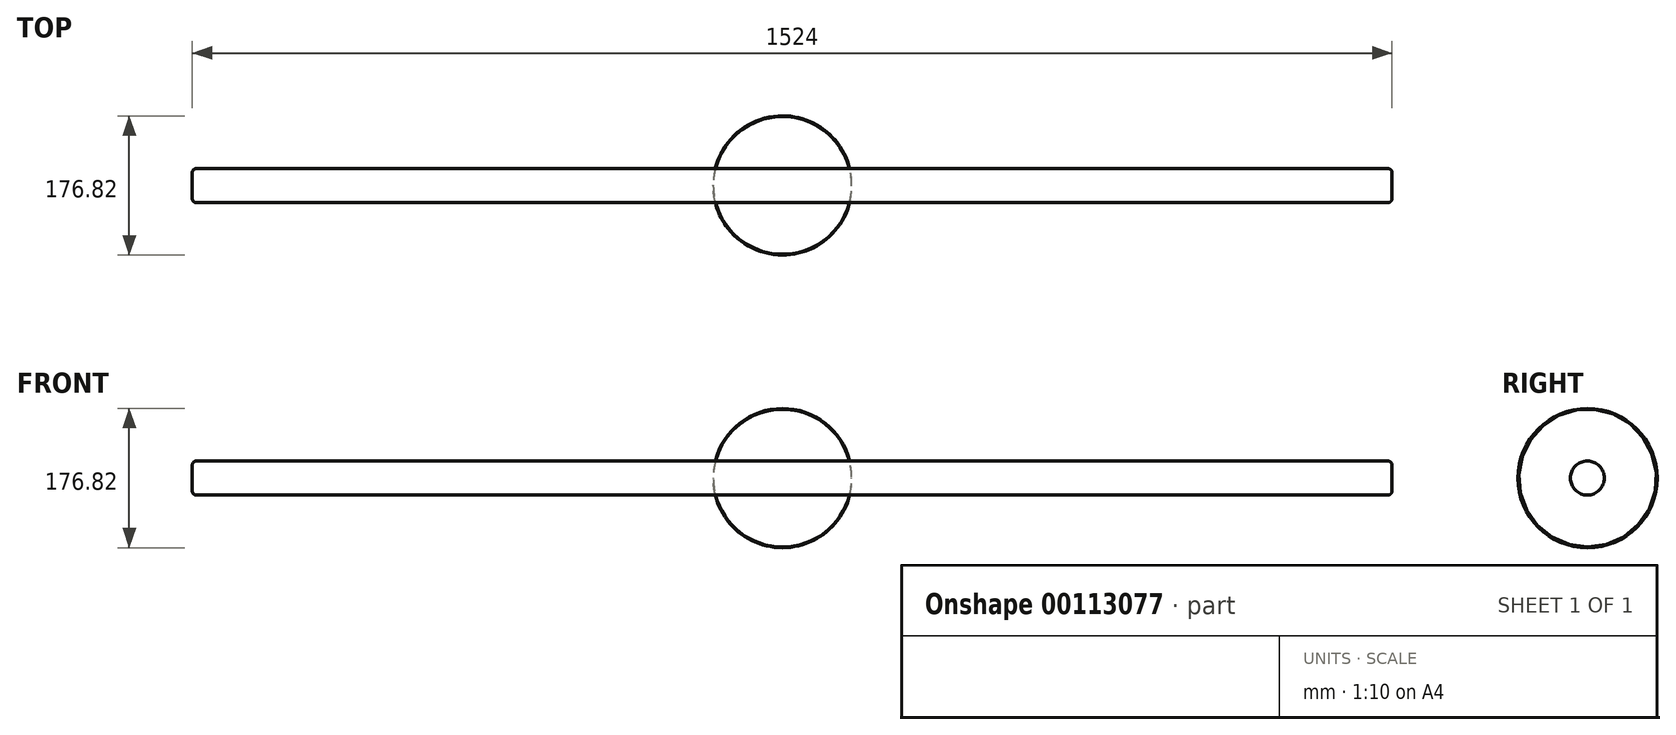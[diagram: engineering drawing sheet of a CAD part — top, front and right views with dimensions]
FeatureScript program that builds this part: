
annotation { "Feature Type Name" : "Feature", "Feature Type Description" : "" }
export const myFeature = defineFeature(function(context is Context, id is Id, definition is map)
    precondition{}
    {
        {
            var Q0;
            Q0=qCreatedBy(makeId("Front.planeOp"),FACE);
            var sketch = newSketch(context, id + "F0", { "sketchPlane" : qUnion([Q0])});
            skLineSegment(sketch, "E0", {"start": v(-87.55, 0) * mm, "end": v(88.32, 0) * mm});
            skArc(sketch, "E1", {"start": v(88.32, 0) * mm, "mid": v(0.38, 87.46) * mm, "end": v(-87.55, 0) * mm});
            skSolve(sketch);
        }
        {
            var Q0;
            Q0 = qSketchRegion(id + "F0", true);
            var Q1;
            Q1=sQuery(id+"F0.wireOp",EDGE,"E0");
            revolve(context, id + "F1", {"entities" : qUnion([Q0]), "axis" : qUnion([Q1]), "revolveType" : RevolveType.FULL});
        }
        {
            var Q0;
            Q0=qCreatedBy(makeId("Right.planeOp"),FACE);
            var sketch = newSketch(context, id + "F2", { "sketchPlane" : qUnion([Q0])});
            skCircle(sketch, "E2", {"center": v(235.25, 11.56) * mm, "radius": 21.62 * mm});
            skSolve(sketch);
        }
        {
            var Q0;
            Q0 = qSketchRegion(id + "F2", true);
            extrude(context, id + "F3", {"entities" : qUnion([Q0]), "depth" : 1524 * mm});
        }
        {
            var Q0;
            Q0=makeQuery(id+"F3.opExtrude","SWEPT_BODY",BODY,{"disambiguationData":[OSD([sQuery(id+"F2.wireOp",EDGE,"E2")])]});
            var Q1;
            Q1=qCreatedBy(makeId("Origin.pointOp"),VERTEX);
            transform(context, id + "F4", {"entities" : qUnion([Q0]), "transformType" : TransformType.TRANSLATION_3D, "dx" : 0 * mm, "dy" : -235.47 * mm, "dz" : -11.48 * mm, "makeCopy" : false});
        }
        {
            var Q0;
            Q0=makeQuery(id+"F1.opRevolve","SWEPT_BODY",BODY,{"disambiguationData":[OSD([sQuery(id+"F0.wireOp",EDGE,"E0"),sQuery(id+"F0.wireOp",EDGE,"E1")])]});
            var Q1;
            Q1=qCreatedBy(makeId("Origin.pointOp"),VERTEX);
            transform(context, id + "F5", {"entities" : qUnion([Q0]), "transformType" : TransformType.TRANSLATION_3D, "dx" : 749.34 * mm, "dy" : 0 * mm, "dz" : 0 * mm, "makeCopy" : false});
        }
        {
            var Q0;
            Q0=makeQuery(id+"F3.opExtrude","CAP_EDGE",EDGE,{"disambiguationData":[OSD([sQuery(id+"F2.wireOp",EDGE,"E2")])],"isStart":true});
            var Q1;
            Q1=makeQuery(id+"F3.opExtrude","CAP_EDGE",EDGE,{"disambiguationData":[OSD([sQuery(id+"F2.wireOp",EDGE,"E2")])],"isStart":false});
            fillet(context, id + "F6", {"entities" : qUnion([Q0, Q1]), "radius" : 5.08 * mm, "tangentPropagation" : true, "allowEdgeOverflow" : false});
        }
    });
